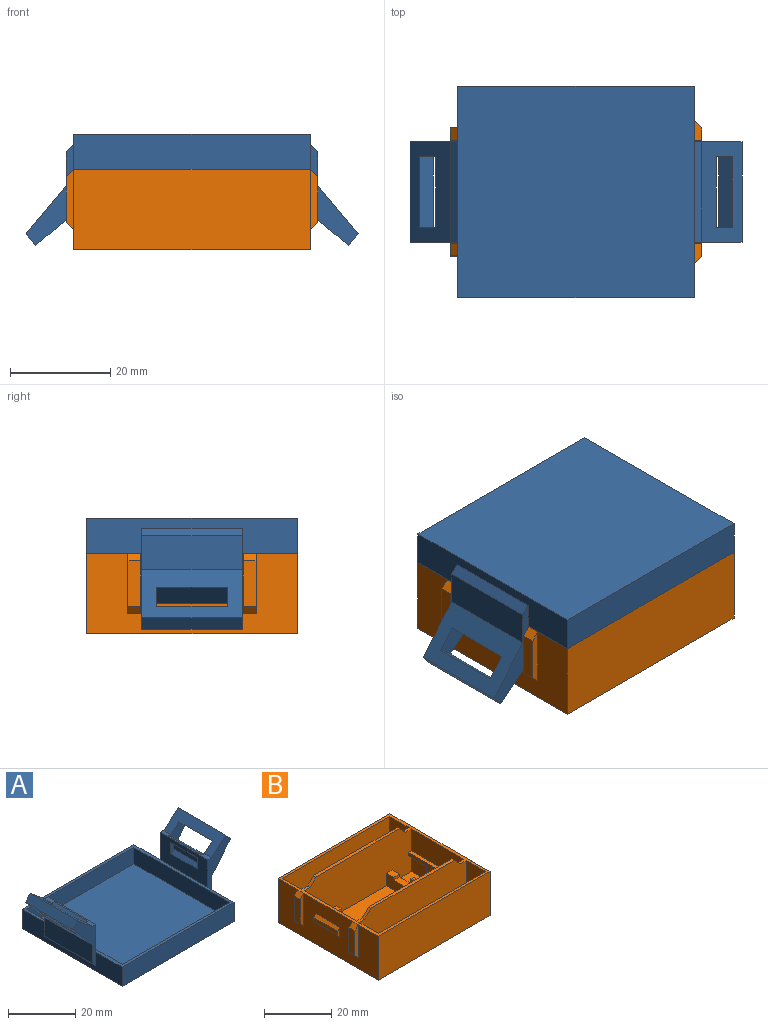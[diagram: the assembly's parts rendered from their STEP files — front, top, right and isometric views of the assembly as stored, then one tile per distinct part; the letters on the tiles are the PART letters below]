
ASSEMBLY  parts=2 mates=1
PART A: 47 faces, bbox 66.1x42x22.1 mm
  f0: plane 4.1x1.2mm, normal (0,1,0), area 3.5mm2, adj f1,f2,f3,f16
  f1: plane 11x1.2mm, normal (0.71,0,-0.71), area 18.7mm2, adj f0,f2,f4,f16
  f2: plane 11x1.7mm, normal (1,0,0), area 18.7mm2, adj f0,f1,f3,f4
  f3: plane 11x1.2mm, normal (0.71,0,0.71), area 18.7mm2, adj f0,f2,f4,f16
  f4: plane 4.1x1.2mm, normal (0,-1,0), area 3.5mm2, adj f1,f2,f3,f16
  f5: plane 14x2.74mm, normal (0.64,0,-0.77), area 50.1mm2, adj f6,f8,f9,f12
  f6: plane 7.13x6.13mm, normal (0,-1,0), area 20.3mm2, adj f5,f7,f9,f10,f12
  f7: plane 14x3.91mm, normal (-0.64,0,0.77), area 71.5mm2, adj f6,f8,f10,f12
  f8: plane 7.13x6.13mm, normal (0,1,0), area 20.3mm2, adj f5,f7,f9,f10,f12
  f9: plane 20x6.13mm, normal (0.64,0,0.77), area 98.1mm2, adj f5,f6,f8,f10,f11,f15,f17
  f10: plane 20x1.5mm, normal (0,0,1), area 16mm2, adj f6,f7,f8,f9,f15,f16,f17
  f11: plane 20x2.3mm, normal (-0.77,0,0.64), area 60mm2, adj f9,f12,f15,f17
  f12: plane 20x9.6mm, normal (-0.77,0,-0.64), area 180.7mm2, adj f5,f6,f7,f8,f11,f13,f15,f17
  f13: plane 20x6.74mm, normal (-1,0,0), area 134.9mm2, adj f12,f14,f15,f17
  f14: plane 20x1.5mm, normal (-0.71,0,-0.71), area 42.4mm2, adj f13,f15,f17,f24
  f15: plane 20.14x9.56mm, normal (0,-1,0), area 60.6mm2, adj f9,f10,f11,f12,f13,f14,f16,f24
  f16: plane 20x10mm, normal (1,0,0), area 154.9mm2, adj f0,f1,f3,f4,f10,f15,f17,f26
  f17: plane 20.14x9.56mm, normal (0,1,0), area 60.6mm2, adj f9,f10,f11,f12,f13,f14,f16,f24
  f18: plane 45x6mm, normal (0,-1,0), area 270mm2, adj f19,f20,f26,f27
  f19: plane 40x6mm, normal (-1,0,0), area 240mm2, adj f18,f21,f26,f27
  f20: plane 40x6mm, normal (1,0,0), area 240mm2, adj f18,f21,f26,f27
  f21: plane 45x6mm, normal (0,1,0), area 270mm2, adj f19,f20,f26,f27
  f22: plane 42x7mm, normal (1,0,0), area 194mm2, adj f23,f25,f26,f28,f43,f44,f46
  f23: plane 47x7mm, normal (0,-1,0), area 329mm2, adj f22,f24,f26,f28
  f24: plane 42x7mm, normal (-1,0,0), area 194mm2, adj f14,f15,f17,f23,f25,f26,f28
  f25: plane 47x7mm, normal (0,1,0), area 329mm2, adj f22,f24,f26,f28
  f26: plane 47x42mm, normal (0,0,1), area 174mm2, adj f16,f18,f19,f20,f21,f22,f23,f24
  f27: plane 45x40mm, normal (0,0,1), area 1800mm2, adj f18,f19,f20,f21
  f28: plane 47x42mm, normal (0,0,-1), area 1974mm2, adj f22,f23,f24,f25
  f29: plane 4.1x1.2mm, normal (0,1,0), area 3.5mm2, adj f30,f31,f32,f45
  f30: plane 11x1.2mm, normal (-0.71,0,-0.71), area 18.7mm2, adj f29,f31,f33,f45
  f31: plane 11x1.7mm, normal (-1,0,0), area 18.7mm2, adj f29,f30,f32,f33
  f32: plane 11x1.2mm, normal (-0.71,0,0.71), area 18.7mm2, adj f29,f31,f33,f45
  f33: plane 4.1x1.2mm, normal (0,-1,0), area 3.5mm2, adj f30,f31,f32,f45
  f34: plane 14x2.74mm, normal (-0.64,0,-0.77), area 50.1mm2, adj f35,f37,f38,f41
  f35: plane 7.13x6.13mm, normal (0,-1,0), area 20.3mm2, adj f34,f36,f38,f39,f41
  f36: plane 14x3.91mm, normal (0.64,0,0.77), area 71.5mm2, adj f35,f37,f39,f41
  f37: plane 7.13x6.13mm, normal (0,1,0), area 20.3mm2, adj f34,f36,f38,f39,f41
  f38: plane 20x6.13mm, normal (-0.64,0,0.77), area 98.1mm2, adj f34,f35,f37,f39,f40,f44,f46
  f39: plane 20x1.5mm, normal (0,0,1), area 16mm2, adj f35,f36,f37,f38,f44,f45,f46
  f40: plane 20x2.3mm, normal (0.77,0,0.64), area 60mm2, adj f38,f41,f44,f46
  f41: plane 20x9.6mm, normal (0.77,0,-0.64), area 180.7mm2, adj f34,f35,f36,f37,f40,f42,f44,f46
  f42: plane 20x6.74mm, normal (1,0,0), area 134.9mm2, adj f41,f43,f44,f46
  f43: plane 20x1.5mm, normal (0.71,0,-0.71), area 42.4mm2, adj f22,f42,f44,f46
  f44: plane 20.14x9.56mm, normal (0,-1,0), area 60.6mm2, adj f22,f38,f39,f40,f41,f42,f43,f45
  f45: plane 20x10mm, normal (-1,0,0), area 154.9mm2, adj f26,f29,f30,f32,f33,f39,f44,f46
  f46: plane 20.14x9.56mm, normal (0,1,0), area 60.6mm2, adj f22,f38,f39,f40,f41,f42,f43,f45
PART B: 96 faces, bbox 50x42x18.6 mm
  f0: plane 47x42mm, normal (0,0,1), area 183.6mm2, adj f5,f10,f20,f21,f26,f32,f34,f35
  f1: plane 9x2.5mm, normal (-1,0,0), area 22.5mm2, adj f2,f3,f4,f5
  f2: plane 2.5x1.5mm, normal (-0.71,0,-0.71), area 5.3mm2, adj f1,f3,f4,f90
  f3: plane 12x1.5mm, normal (0,1,0), area 15.8mm2, adj f1,f2,f5,f90
  f4: plane 12x1.5mm, normal (0,-1,0), area 15.8mm2, adj f1,f2,f5,f90
  f5: plane 2.5x1.5mm, normal (-0.71,0,0.71), area 5.3mm2, adj f0,f1,f3,f4
  f6: plane 9x2.5mm, normal (-1,0,0), area 22.5mm2, adj f7,f8,f9,f10
  f7: plane 2.5x1.5mm, normal (-0.71,0,-0.71), area 5.3mm2, adj f6,f8,f9,f90
  f8: plane 12x1.5mm, normal (0,1,0), area 15.8mm2, adj f6,f7,f10,f90
  f9: plane 12x1.5mm, normal (0,-1,0), area 15.7mm2, adj f6,f7,f10,f90
  f10: plane 2.5x1.5mm, normal (-0.71,0,0.71), area 5.3mm2, adj f0,f6,f8,f9
  f11: plane 10x1.5mm, normal (-1,0,0), area 15mm2, adj f12,f13,f14,f15
  f12: plane 3.5x1mm, normal (0,1,0), area 2.5mm2, adj f11,f13,f14,f90
  f13: plane 10x1mm, normal (-0.71,0,0.71), area 14.1mm2, adj f11,f12,f15,f90
  f14: plane 10x1mm, normal (-0.71,0,-0.71), area 14.1mm2, adj f11,f12,f15,f90
  f15: plane 3.5x1mm, normal (0,-1,0), area 2.5mm2, adj f11,f13,f14,f90
  f16: plane 9x2.5mm, normal (1,0,0), area 22.5mm2, adj f17,f18,f19,f20
  f17: plane 4x1.5mm, normal (0.71,0,-0.71), area 6.9mm2, adj f16,f18,f19,f21
  f18: plane 12x1.5mm, normal (0.71,-0.71,0), area 22.3mm2, adj f16,f17,f20,f21
  f19: plane 12x1.5mm, normal (0,1,0), area 15.8mm2, adj f16,f17,f20,f21
  f20: plane 4x1.5mm, normal (0.71,0,0.71), area 6.9mm2, adj f0,f16,f18,f19
  f21: plane 42x16mm, normal (1,0,0), area 541mm2, adj f0,f17,f18,f19,f23,f24,f25,f28
  f22: plane 9x2.5mm, normal (1,0,0), area 22.5mm2, adj f23,f24,f25,f26
  f23: plane 4x1.5mm, normal (0.71,0,-0.71), area 6.9mm2, adj f21,f22,f24,f25
  f24: plane 12x1.5mm, normal (0,-1,0), area 15.8mm2, adj f21,f22,f23,f26
  f25: plane 12x1.5mm, normal (0.71,0.71,0), area 22.3mm2, adj f21,f22,f23,f26
  f26: plane 4x1.5mm, normal (0.71,0,0.71), area 6.9mm2, adj f0,f22,f24,f25
  f27: plane 10x1.5mm, normal (1,0,0), area 15mm2, adj f28,f29,f30,f31
  f28: plane 3.5x1mm, normal (0,1,0), area 2.5mm2, adj f21,f27,f29,f30
  f29: plane 10x1mm, normal (0.71,0,0.71), area 14.1mm2, adj f21,f27,f28,f31
  f30: plane 10x1mm, normal (0.71,0,-0.71), area 14.1mm2, adj f21,f27,f28,f31
  f31: plane 3.5x1mm, normal (0,-1,0), area 2.5mm2, adj f21,f27,f29,f30
  f32: plane 47x16mm, normal (0,1,0), area 752mm2, adj f0,f21,f33,f90
  f33: plane 47x42mm, normal (0,0,-1), area 1974mm2, adj f21,f32,f34,f90
  f34: plane 47x16mm, normal (0,-1,0), area 752mm2, adj f0,f21,f33,f90
  f35: plane 45x18mm, normal (0,-1,0), area 790.8mm2, adj f0,f36,f83,f87,f91,f94,f95
  f36: plane 45x8mm, normal (0,0,1), area 360mm2, adj f35,f82,f83,f87
  f37: plane 45x18mm, normal (0,1,0), area 756.3mm2, adj f0,f50,f52,f53,f54,f58,f60,f69
  f38: plane 45x15.4mm, normal (0,-1,0), area 693mm2, adj f0,f77,f84,f88
  f39: plane 7.5x1.3mm, normal (-0.71,0,-0.71), area 13.8mm2, adj f40,f42,f47,f86
  f40: plane 45x18mm, normal (0,-1,0), area 730.7mm2, adj f0,f39,f41,f47,f49,f51,f68,f69
  f41: plane 14.5x1.3mm, normal (0,0,1), area 18.8mm2, adj f40,f47,f48,f85
  f42: plane 8x6.31mm, normal (0,1,0), area 16.1mm2, adj f39,f43,f44,f45,f46,f47,f49,f51
  f43: plane 7x1.41mm, normal (-0.98,0,0.21), area 10.1mm2, adj f42,f44,f48,f67
  f44: plane 7x1mm, normal (0,0,1), area 7mm2, adj f42,f43,f45,f48
  f45: plane 7x0.4mm, normal (1,0,0), area 2.8mm2, adj f42,f44,f46,f48
  f46: cylinder r=3mm len=7mm, axis (0,-1,0), area 84.9mm2, adj f42,f45,f47,f48
  f47: plane 14.5x3mm, normal (-1,0,0), area 30mm2, adj f39,f40,f41,f42,f46,f48
  f48: plane 8x7.51mm, normal (0,-1,0), area 18.5mm2, adj f41,f43,f44,f45,f46,f47,f50,f52
  f49: plane 8x7.5mm, normal (0,0,1), area 60mm2, adj f40,f42,f51,f86
  f50: plane 8x7.5mm, normal (0,0,1), area 60mm2, adj f37,f48,f52,f85
  f51: plane 7.5x4.5mm, normal (1,0,0), area 29.3mm2, adj f40,f42,f49,f65,f67,f71
  f52: plane 7.5x5.5mm, normal (1,0,0), area 37mm2, adj f37,f48,f50,f59,f60,f66,f67,f72
  f53: plane 3.5x1mm, normal (0,0.71,-0.71), area 4.9mm2, adj f37,f54,f55,f69
  f54: plane 2x1mm, normal (1,0,0), area 1.5mm2, adj f37,f53,f55,f81
  f55: plane 3.5x1mm, normal (0,1,0), area 3.5mm2, adj f53,f54,f69,f81
  f56: plane 11x1mm, normal (0,-0.71,-0.71), area 15.6mm2, adj f69,f73,f78,f79
  f57: plane 2.5x1mm, normal (0,1,0), area 2.5mm2, adj f58,f61,f69,f89
  f58: plane 4.5x2.5mm, normal (0,0,1), area 11.2mm2, adj f37,f57,f69,f89
  f59: plane 2.5x1mm, normal (0,1,0), area 2.5mm2, adj f52,f60,f70,f72
  f60: plane 4.5x2.5mm, normal (0,0,1), area 11.2mm2, adj f37,f52,f59,f70
  f61: plane 2.5x1.7mm, normal (0,0,1), area 4.3mm2, adj f57,f62,f69,f89
  f62: plane 2.5x1mm, normal (0,1,0), area 2.5mm2, adj f61,f64,f69,f89
  f63: plane 2.5x1mm, normal (0,-1,0), area 2.5mm2, adj f64,f68,f69,f89
  f64: plane 12.8x2.5mm, normal (0,0,1), area 32mm2, adj f62,f63,f69,f89
  f65: plane 2.5x1mm, normal (0,-1,0), area 2.5mm2, adj f51,f67,f70,f71
  f66: plane 2.5x1mm, normal (0,1,0), area 2.5mm2, adj f52,f67,f70,f72
  f67: plane 12.8x2.5mm, normal (0,0,1), area 32mm2, adj f43,f51,f52,f65,f66,f70
  f68: plane 3x2.5mm, normal (0,0,1), area 7.5mm2, adj f40,f63,f69,f89
  f69: plane 22x5.5mm, normal (1,0,0), area 84.5mm2, adj f37,f40,f53,f55,f56,f57,f58,f61
  f70: plane 22x5.5mm, normal (-1,0,0), area 90.7mm2, adj f37,f40,f59,f60,f65,f66,f67,f71
  f71: plane 3x2.5mm, normal (0,0,1), area 7.5mm2, adj f40,f51,f65,f70
  f72: plane 2.5x1.7mm, normal (0,0,1), area 4.3mm2, adj f52,f59,f66,f70
  f73: plane 11x1.2mm, normal (0,-1,0), area 13.2mm2, adj f56,f69,f74,f78
  f74: plane 32x22mm, normal (0,0,1), area 693mm2, adj f37,f40,f69,f70,f73,f78
  f75: plane 45x18mm, normal (0,1,0), area 790.8mm2, adj f0,f76,f77,f84,f88,f92,f93
  f76: plane 35x1mm, normal (0,0,1), area 35mm2, adj f40,f75,f92,f93
  f77: plane 45x8mm, normal (0,0,1), area 360mm2, adj f38,f75,f84,f88
  f78: plane 3.2x2mm, normal (1,0,0), area 4.7mm2, adj f40,f56,f73,f74,f79,f80
  f79: plane 11x1mm, normal (0,-1,0), area 11mm2, adj f56,f69,f78,f80
  f80: plane 11x2mm, normal (0,0,1), area 22mm2, adj f40,f69,f78,f79
  f81: plane 3.5x1mm, normal (0,0,1), area 3.5mm2, adj f37,f54,f55,f69
  f82: plane 45x15.4mm, normal (0,1,0), area 693mm2, adj f0,f36,f83,f87
  f83: plane 15.4x8mm, normal (-1,0,0), area 123.2mm2, adj f0,f35,f36,f82
  f84: plane 15.4x8mm, normal (-1,0,0), area 123.2mm2, adj f0,f38,f75,f77
  f85: plane 22x15.4mm, normal (-1,0,0), area 229.9mm2, adj f0,f37,f40,f41,f48,f50
  f86: plane 7.5x5.01mm, normal (-1,0,0), area 37.6mm2, adj f39,f40,f42,f49
  f87: plane 15.4x8mm, normal (1,0,0), area 123.2mm2, adj f0,f35,f36,f82
  f88: plane 15.4x8mm, normal (1,0,0), area 123.2mm2, adj f0,f38,f75,f77
  f89: plane 22x11.9mm, normal (1,0,0), area 248.1mm2, adj f0,f37,f40,f57,f58,f61,f62,f63
  f90: plane 42x16mm, normal (-1,0,0), area 577mm2, adj f0,f2,f3,f4,f7,f8,f9,f12
  f91: plane 35x1mm, normal (0,0,1), area 35mm2, adj f35,f37,f94,f95
  f92: plane 2.6x2.6mm, normal (0.71,0,0.71), area 3.7mm2, adj f0,f40,f75,f76
  f93: plane 2.6x2.6mm, normal (-0.71,0,0.71), area 3.7mm2, adj f0,f40,f75,f76
  f94: plane 2.6x2.6mm, normal (0.71,0,0.71), area 3.7mm2, adj f0,f35,f37,f91
  f95: plane 2.6x2.6mm, normal (-0.71,0,0.71), area 3.7mm2, adj f0,f35,f37,f91
PLACE A rot(axis=(1,0,0),180deg) t=(54.48,35.99,13.39)mm
PLACE B t=(31.98,20.49,-9.01)mm
MATE fastened A.f26 <-> B.f0  axis (0,0,-1) through (30.98,14.99,6.39)mm
